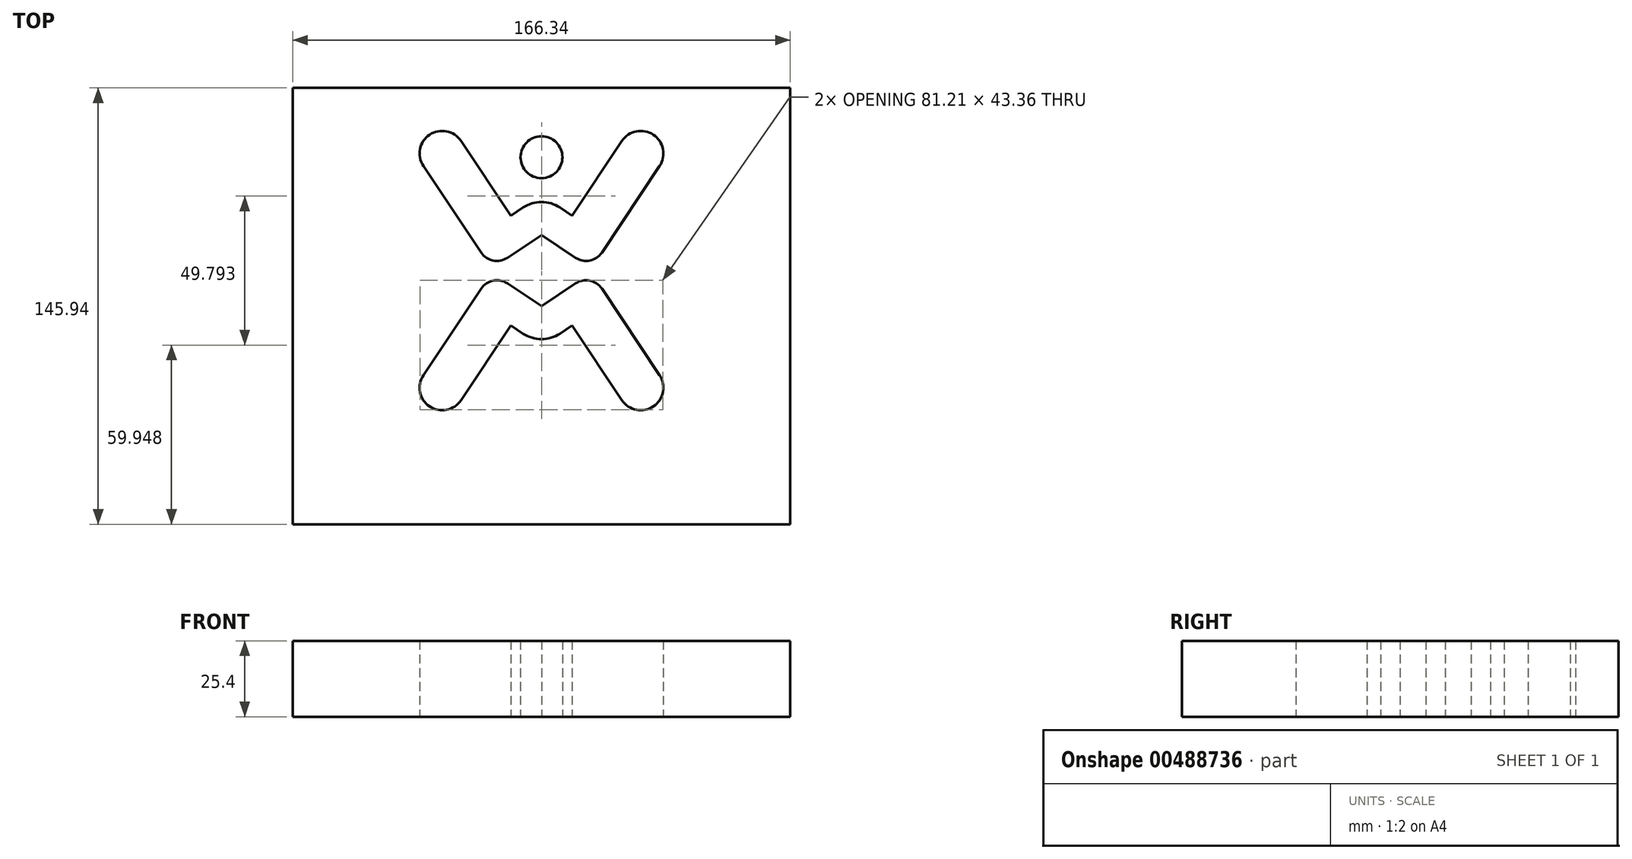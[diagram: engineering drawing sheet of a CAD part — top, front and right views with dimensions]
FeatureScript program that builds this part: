
annotation { "Feature Type Name" : "Feature", "Feature Type Description" : "" }
export const myFeature = defineFeature(function(context is Context, id is Id, definition is map)
    precondition{}
    {
        {
            var Q0;
            Q0=qCreatedBy(makeId("Top.planeOp"),FACE);
            var sketch = newSketch(context, id + "F0", { "sketchPlane" : qUnion([Q0])});
            skLineSegment(sketch, "E0.bottom", {"start": v(-83.17, 72.97) * mm, "end": v(83.17, 72.97) * mm});
            skLineSegment(sketch, "E0.top", {"start": v(-83.17, -72.97) * mm, "end": v(83.17, -72.97) * mm});
            skLineSegment(sketch, "E0.left", {"start": v(-83.17, 72.97) * mm, "end": v(-83.17, -72.97) * mm});
            skLineSegment(sketch, "E0.right", {"start": v(83.17, 72.97) * mm, "end": v(83.17, -72.97) * mm});
            skPoint(sketch, "E0.middle", {"position": v(0, 0) * mm});
            skSolve(sketch);
        }
        {
            var Q0;
            Q0 = qSketchRegion(id + "F0", true);
            extrude(context, id + "F1", {"entities" : qUnion([Q0]), "depth" : 25.4 * mm});
        }
        {
            var Q0;
            Q0=qCreatedBy(makeId("Top.planeOp"),FACE);
            var sketch = newSketch(context, id + "F2", { "sketchPlane" : qUnion([Q0])});
            skLineSegment(sketch, "E1.bottom", {"start": v(-4.1, 2.74) * mm, "end": v(-11.39, 7.6) * mm});
            skLineSegment(sketch, "E1.top", {"start": v(-26.91, -31.48) * mm, "end": v(-39.48, -23.1) * mm});
            skLineSegment(sketch, "E1.left", {"start": v(-4.1, 2.74) * mm, "end": v(-26.91, -31.48) * mm});
            skLineSegment(sketch, "E1.right", {"start": v(-20.2, 5.83) * mm, "end": v(-39.48, -23.1) * mm});
            skLineSegment(sketch, "E2.bottom", {"start": v(-10.24, -6.47) * mm, "end": v(-4.1, 2.74) * mm});
            skLineSegment(sketch, "E2.top", {"start": v(-6.14, -9.2) * mm, "end": v(0, 0) * mm});
            skLineSegment(sketch, "E2.left", {"start": v(-6.14, -9.2) * mm, "end": v(-10.24, -6.47) * mm});
            skLineSegment(sketch, "E2.right", {"start": v(0, 0) * mm, "end": v(-4.1, 2.74) * mm});
            skLineSegment(sketch, "E3", {"start": v(0, 0) * mm, "end": v(0, -40.07) * mm, "construction": true});
            skLineSegment(sketch, "E4.MirrorCS", {"start": v(0, 0) * mm, "end": v(4.1, 2.74) * mm});
            skLineSegment(sketch, "E5.MirrorCS", {"start": v(6.14, -9.2) * mm, "end": v(10.24, -6.47) * mm});
            skLineSegment(sketch, "E6.MirrorCS", {"start": v(4.1, 2.74) * mm, "end": v(11.39, 7.6) * mm});
            skLineSegment(sketch, "E7.MirrorCS", {"start": v(6.14, -9.2) * mm, "end": v(0, 0) * mm});
            skLineSegment(sketch, "E8.MirrorCS", {"start": v(10.24, -6.47) * mm, "end": v(4.1, 2.74) * mm});
            skLineSegment(sketch, "E9.MirrorCS", {"start": v(20.2, 5.83) * mm, "end": v(39.48, -23.1) * mm});
            skLineSegment(sketch, "E10.MirrorCS", {"start": v(4.1, 2.74) * mm, "end": v(26.91, -31.48) * mm});
            skLineSegment(sketch, "E11.MirrorCS", {"start": v(26.91, -31.48) * mm, "end": v(39.48, -23.1) * mm});
            skCircle(sketch, "E12", {"center": v(0, 49.8) * mm, "radius": 7 * mm});
            skArc(sketch, "E13", {"start": v(6.14, -9.2) * mm, "mid": v(0, -11.07) * mm, "end": v(-6.14, -9.2) * mm});
            skArc(sketch, "E14", {"start": v(-39.48, -23.1) * mm, "mid": v(-37.39, -33.58) * mm, "end": v(-26.91, -31.48) * mm});
            skArc(sketch, "E15", {"start": v(26.91, -31.48) * mm, "mid": v(37.39, -33.58) * mm, "end": v(39.48, -23.1) * mm});
            skLineSegment(sketch, "E16", {"start": v(21.02, 11.87) * mm, "end": v(-19.34, 11.87) * mm, "construction": true});
            skLineSegment(sketch, "E17.MirrorCS", {"start": v(-6.14, 32.96) * mm, "end": v(0, 23.75) * mm});
            skLineSegment(sketch, "E18.MirrorCS", {"start": v(0, 23.75) * mm, "end": v(4.1, 21.01) * mm});
            skLineSegment(sketch, "E19.MirrorCS", {"start": v(-10.24, 30.22) * mm, "end": v(-4.1, 21.01) * mm});
            skLineSegment(sketch, "E20.MirrorCS", {"start": v(10.24, 30.22) * mm, "end": v(4.1, 21.01) * mm});
            skLineSegment(sketch, "E21.MirrorCS", {"start": v(0, 23.75) * mm, "end": v(0, 63.82) * mm, "construction": true});
            skLineSegment(sketch, "E22.MirrorCS", {"start": v(-4.1, 21.01) * mm, "end": v(-11.39, 16.16) * mm});
            skLineSegment(sketch, "E23.MirrorCS", {"start": v(-6.14, 32.96) * mm, "end": v(-10.24, 30.22) * mm});
            skArc(sketch, "E24.MirrorCS", {"start": v(6.14, 32.96) * mm, "mid": v(0, 34.82) * mm, "end": v(-6.14, 32.96) * mm});
            skLineSegment(sketch, "E25.MirrorCS", {"start": v(4.1, 21.01) * mm, "end": v(11.39, 16.16) * mm});
            skLineSegment(sketch, "E26.MirrorCS", {"start": v(6.14, 32.96) * mm, "end": v(10.24, 30.22) * mm});
            skLineSegment(sketch, "E27.MirrorCS", {"start": v(-20.2, 17.92) * mm, "end": v(-39.48, 46.85) * mm});
            skLineSegment(sketch, "E28.MirrorCS", {"start": v(6.14, 32.96) * mm, "end": v(0, 23.75) * mm});
            skLineSegment(sketch, "E29.MirrorCS", {"start": v(26.91, 55.23) * mm, "end": v(39.48, 46.85) * mm});
            skLineSegment(sketch, "E30.MirrorCS", {"start": v(4.1, 21.01) * mm, "end": v(26.91, 55.23) * mm});
            skLineSegment(sketch, "E31.MirrorCS", {"start": v(0, 23.75) * mm, "end": v(-4.1, 21.01) * mm});
            skLineSegment(sketch, "E32.MirrorCS", {"start": v(20.2, 17.92) * mm, "end": v(39.48, 46.85) * mm});
            skArc(sketch, "E33.MirrorCS", {"start": v(-39.48, 46.85) * mm, "mid": v(-37.39, 57.33) * mm, "end": v(-26.91, 55.23) * mm});
            skArc(sketch, "E34.MirrorCS", {"start": v(26.91, 55.23) * mm, "mid": v(37.39, 57.33) * mm, "end": v(39.48, 46.85) * mm});
            skLineSegment(sketch, "E35.MirrorCS", {"start": v(-26.91, 55.23) * mm, "end": v(-39.48, 46.85) * mm});
            skLineSegment(sketch, "E36.MirrorCS", {"start": v(-4.1, 21.01) * mm, "end": v(-26.91, 55.23) * mm});
            skPoint(sketch, "E37.visualSharp", {"position": v(-16.67, 11.11) * mm});
            skArc(sketch, "E37.filletArc", {"start": v(-11.39, 7.6) * mm, "mid": v(-16.15, 8.53) * mm, "end": v(-20.2, 5.83) * mm});
            skPoint(sketch, "E38.visualSharp", {"position": v(16.67, 11.11) * mm});
            skArc(sketch, "E38.filletArc", {"start": v(20.2, 5.83) * mm, "mid": v(16.15, 8.53) * mm, "end": v(11.39, 7.6) * mm});
            skPoint(sketch, "E39.visualSharp", {"position": v(16.67, 12.64) * mm});
            skArc(sketch, "E39.filletArc", {"start": v(11.39, 16.16) * mm, "mid": v(16.15, 15.22) * mm, "end": v(20.2, 17.92) * mm});
            skPoint(sketch, "E40.visualSharp", {"position": v(-16.67, 12.64) * mm});
            skArc(sketch, "E40.filletArc", {"start": v(-20.2, 17.92) * mm, "mid": v(-16.15, 15.22) * mm, "end": v(-11.39, 16.16) * mm});
            skSolve(sketch);
        }
        {
            var Q0;
            Q0 = qSketchRegion(id + "F2", true);
            extrude(context, id + "F3", {"entities" : qUnion([Q0]), "operationType" : NewBodyOperationType.REMOVE, "depth" : 87.88 * mm});
        }
    });
